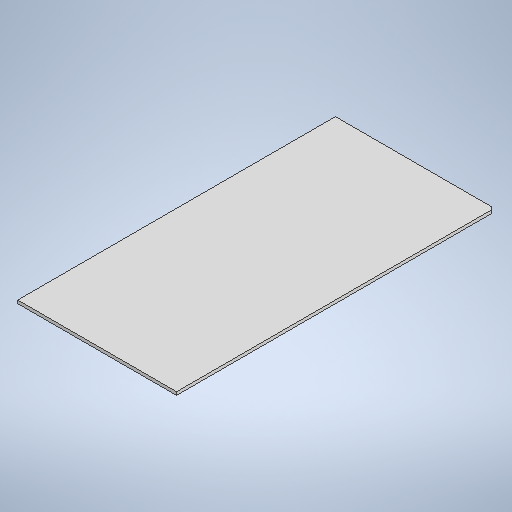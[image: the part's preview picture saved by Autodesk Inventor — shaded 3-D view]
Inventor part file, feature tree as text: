
AUTODESK INVENTOR PART (.ipt)
format: ipt  version: 2025 (Build 290162010, 162A)  size: 291,840 bytes
history: native  units: mm
features: other x3, sketch x2, sheet_metal_op x1, chamfer x1
ambient origin geometry x8: Origin, YZ Plane, XZ Plane, XY Plane, X Axis, Y Axis, Z Axis, Center Point
bodies: Solid1 (feature_tree)
feature tree (7):
  sheet_metal_op  "Face1"
  chamfer  "Chamfer1"  Distance=2.0mm
  other  "Mark1"
  sketch  "Sketch1"  dims[d0=100.0mm]
  other  "Plate1"
  sketch  "Sketch2"  dims[d1=200.0mm d2=2.0mm d3=2.0mm d4=2.0mm d5=45.0deg]
  other  "Definition1"
